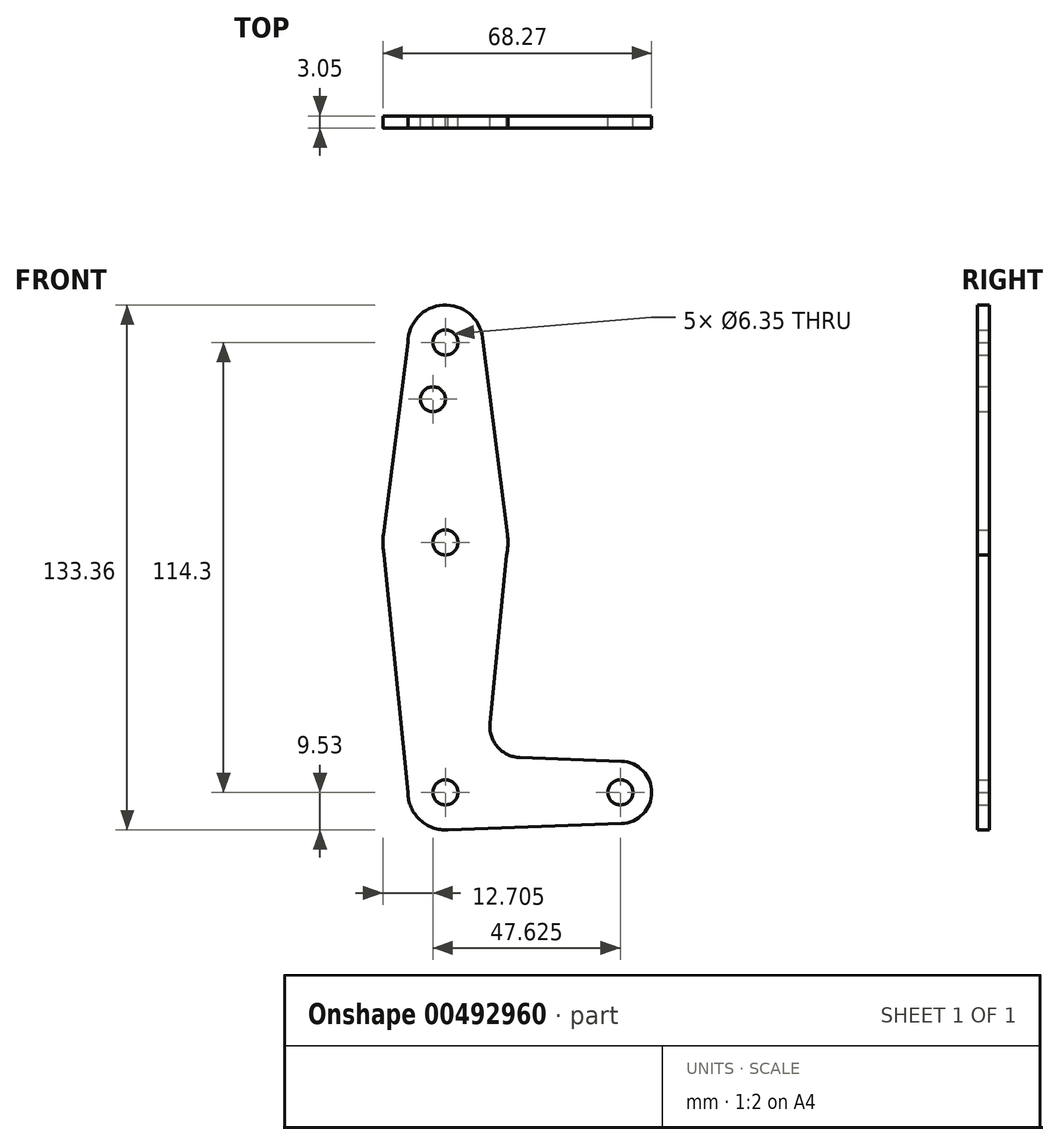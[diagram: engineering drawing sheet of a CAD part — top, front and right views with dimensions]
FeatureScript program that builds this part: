
annotation { "Feature Type Name" : "Feature", "Feature Type Description" : "" }
export const myFeature = defineFeature(function(context is Context, id is Id, definition is map)
    precondition{}
    {
        {
            var Q0;
            Q0=qCreatedBy(makeId("Front.planeOp"),FACE);
            var sketch = newSketch(context, id + "F0", { "sketchPlane" : qUnion([Q0])});
            skLineSegment(sketch, "E0", {"start": v(0, 0) * mm, "end": v(0, 114.3) * mm, "construction": true});
            skLineSegment(sketch, "E1", {"start": v(0, 0) * mm, "end": v(44.45, 0) * mm});
            skCircle(sketch, "E2", {"center": v(0, 0) * mm, "radius": 9.53 * mm});
            skCircle(sketch, "E3", {"center": v(0, 114.3) * mm, "radius": 9.53 * mm});
            skCircle(sketch, "E4", {"center": v(44.45, 0) * mm, "radius": 7.94 * mm});
            skCircle(sketch, "E5", {"center": v(0, 63.5) * mm, "radius": 15.88 * mm});
            skLineSegment(sketch, "E6", {"start": v(-9.53, 114.3) * mm, "end": v(-15.75, 65.5) * mm});
            skLineSegment(sketch, "E7", {"start": v(9.45, 115.5) * mm, "end": v(15.75, 65.48) * mm});
            skLineSegment(sketch, "E8", {"start": v(18.95, 8.85) * mm, "end": v(44.73, 7.93) * mm});
            skLineSegment(sketch, "E9", {"start": v(0, -9.53) * mm, "end": v(44.73, -7.93) * mm});
            skLineSegment(sketch, "E10", {"start": v(-15.87, 63.5) * mm, "end": v(-9.53, 0) * mm});
            skLineSegment(sketch, "E11", {"start": v(15.88, 63.5) * mm, "end": v(11.32, 17.58) * mm});
            skArc(sketch, "E12.filletArc", {"start": v(11.32, 17.58) * mm, "mid": v(13.24, 11.56) * mm, "end": v(18.95, 8.85) * mm});
            skCircle(sketch, "E13", {"center": v(0, 114.3) * mm, "radius": 3.18 * mm});
            skCircle(sketch, "E14", {"center": v(0, 63.5) * mm, "radius": 3.18 * mm});
            skCircle(sketch, "E15", {"center": v(-3.18, 99.89) * mm, "radius": 3.18 * mm});
            skCircle(sketch, "E16", {"center": v(0, 0) * mm, "radius": 3.18 * mm});
            skCircle(sketch, "E17", {"center": v(44.45, 0) * mm, "radius": 3.18 * mm});
            skSolve(sketch);
        }
        {
            var Q0;
            Q0 = qSketchRegion(id + "F0", true);
            extrude(context, id + "F1", {"entities" : qUnion([Q0]), "depth" : 3.05 * mm});
        }
    });
